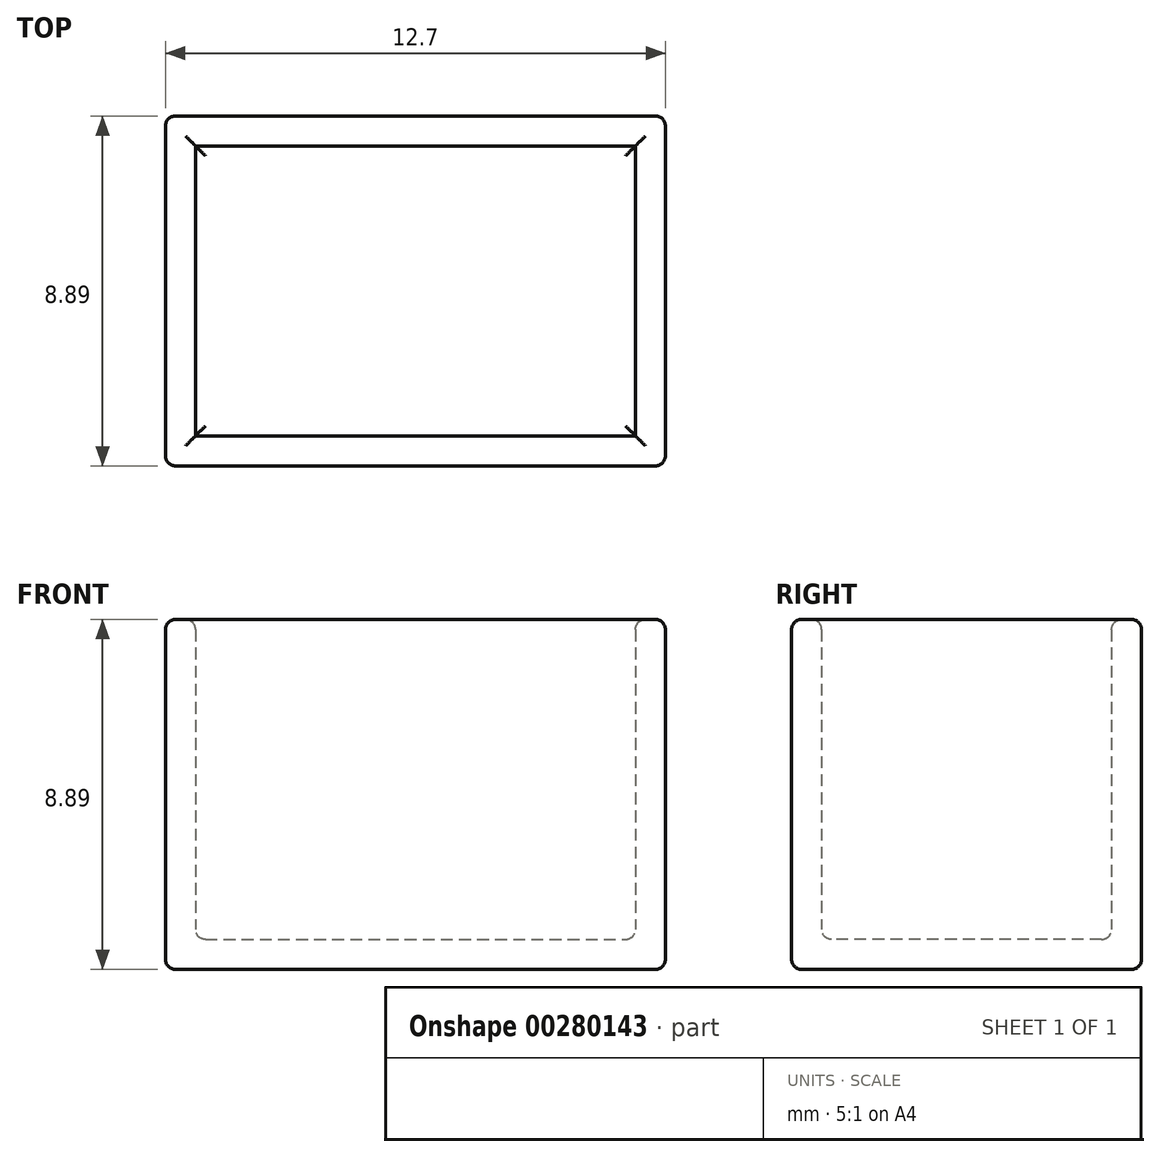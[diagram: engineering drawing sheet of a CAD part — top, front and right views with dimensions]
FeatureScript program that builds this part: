
annotation { "Feature Type Name" : "Feature", "Feature Type Description" : "" }
export const myFeature = defineFeature(function(context is Context, id is Id, definition is map)
    precondition{}
    {
        {
            var Q0;
            Q0=qCreatedBy(makeId("Top.planeOp"),FACE);
            var sketch = newSketch(context, id + "F0", { "sketchPlane" : qUnion([Q0])});
            skLineSegment(sketch, "E0.bottom", {"start": v(-47.71, 34.6) * mm, "end": v(-35.01, 34.6) * mm});
            skLineSegment(sketch, "E0.top", {"start": v(-47.71, 25.7) * mm, "end": v(-35.01, 25.7) * mm});
            skLineSegment(sketch, "E0.left", {"start": v(-47.71, 34.6) * mm, "end": v(-47.71, 25.7) * mm});
            skLineSegment(sketch, "E0.right", {"start": v(-35.01, 34.6) * mm, "end": v(-35.01, 25.7) * mm});
            skSolve(sketch);
        }
        {
            var Q0;
            Q0 = qSketchRegion(id + "F0", true);
            extrude(context, id + "F1", {"entities" : qUnion([Q0]), "depth" : 8.9 * mm});
        }
        {
            var Q0;
            Q0=makeQuery(id+"F1.opExtrude","CAP_FACE",FACE,{"disambiguationData":[OSD([sQuery(id+"F0.wireOp",EDGE,"E0.bottom"),sQuery(id+"F0.wireOp",EDGE,"E0.top"),sQuery(id+"F0.wireOp",EDGE,"E0.left"),sQuery(id+"F0.wireOp",EDGE,"E0.right")])],"isStart":false});
            shell(context, id + "F2", {"entities" : qUnion([Q0]), "thickness" : 0.76 * mm});
        }
        {
            var Q0;
            {var subQ0=sQuery(id+"F0.wireOp",EDGE,"E0.bottom");Q0=makeQuery(id+"F2.opShell","OFFSET_EDGE",EDGE,{"disambiguationData":[OSD([subQ0]),TDD([makeQuery(id+"F1.opExtrude","CAP_EDGE",EDGE,{"disambiguationData":[OSD([subQ0])],"isStart":false})])]});}
            var Q1;
            Q1=makeQuery(id+"F1.opExtrude","CAP_EDGE",EDGE,{"disambiguationData":[OSD([sQuery(id+"F0.wireOp",EDGE,"E0.top")])],"isStart":false});
            var Q2;
            {var subQ0=sQuery(id+"F0.wireOp",EDGE,"E0.top");Q2=makeQuery(id+"F2.opShell","OFFSET_EDGE",EDGE,{"disambiguationData":[OSD([subQ0]),TDD([makeQuery(id+"F1.opExtrude","CAP_EDGE",EDGE,{"disambiguationData":[OSD([subQ0])],"isStart":false})])]});}
            var Q3;
            Q3=makeQuery(id+"F1.opExtrude","CAP_EDGE",EDGE,{"disambiguationData":[OSD([sQuery(id+"F0.wireOp",EDGE,"E0.bottom")])],"isStart":false});
            var Q4;
            {var subQ0=sQuery(id+"F0.wireOp",EDGE,"E0.left");Q4=makeQuery(id+"F2.opShell","OFFSET_EDGE",EDGE,{"disambiguationData":[OSD([subQ0]),TDD([makeQuery(id+"F1.opExtrude","CAP_EDGE",EDGE,{"disambiguationData":[OSD([subQ0])],"isStart":false})])]});}
            var Q5;
            Q5=makeQuery(id+"F1.opExtrude","CAP_EDGE",EDGE,{"disambiguationData":[OSD([sQuery(id+"F0.wireOp",EDGE,"E0.left")])],"isStart":false});
            var Q6;
            {var subQ0=sQuery(id+"F0.wireOp",EDGE,"E0.right");Q6=makeQuery(id+"F2.opShell","OFFSET_EDGE",EDGE,{"disambiguationData":[OSD([subQ0]),TDD([makeQuery(id+"F1.opExtrude","CAP_EDGE",EDGE,{"disambiguationData":[OSD([subQ0])],"isStart":false})])]});}
            var Q7;
            Q7=makeQuery(id+"F1.opExtrude","CAP_EDGE",EDGE,{"disambiguationData":[OSD([sQuery(id+"F0.wireOp",EDGE,"E0.right")])],"isStart":false});
            var Q8;
            Q8=makeQuery(id+"F1.opExtrude","SWEPT_EDGE",EDGE,{"disambiguationData":[OSD([sQuery(id+"F0.wireOp",EDGE,"E0.top"),sQuery(id+"F0.wireOp",EDGE,"E0.right")])]});
            var Q9;
            Q9=makeQuery(id+"F1.opExtrude","SWEPT_EDGE",EDGE,{"disambiguationData":[OSD([sQuery(id+"F0.wireOp",EDGE,"E0.top"),sQuery(id+"F0.wireOp",EDGE,"E0.left")])]});
            var Q10;
            Q10=makeQuery(id+"F1.opExtrude","SWEPT_EDGE",EDGE,{"disambiguationData":[OSD([sQuery(id+"F0.wireOp",EDGE,"E0.bottom"),sQuery(id+"F0.wireOp",EDGE,"E0.left")])]});
            var Q11;
            Q11=makeQuery(id+"F1.opExtrude","SWEPT_EDGE",EDGE,{"disambiguationData":[OSD([sQuery(id+"F0.wireOp",EDGE,"E0.bottom"),sQuery(id+"F0.wireOp",EDGE,"E0.right")])]});
            var Q12;
            Q12=makeQuery(id+"F1.opExtrude","CAP_EDGE",EDGE,{"disambiguationData":[OSD([sQuery(id+"F0.wireOp",EDGE,"E0.right")])],"isStart":true});
            var Q13;
            Q13=makeQuery(id+"F1.opExtrude","CAP_EDGE",EDGE,{"disambiguationData":[OSD([sQuery(id+"F0.wireOp",EDGE,"E0.top")])],"isStart":true});
            var Q14;
            Q14=makeQuery(id+"F1.opExtrude","CAP_EDGE",EDGE,{"disambiguationData":[OSD([sQuery(id+"F0.wireOp",EDGE,"E0.left")])],"isStart":true});
            var Q15;
            Q15=makeQuery(id+"F1.opExtrude","CAP_EDGE",EDGE,{"disambiguationData":[OSD([sQuery(id+"F0.wireOp",EDGE,"E0.bottom")])],"isStart":true});
            fillet(context, id + "F3", {"entities" : qUnion([Q0, Q1, Q2, Q3, Q4, Q5, Q6, Q7, Q8, Q9, Q10, Q11, Q12, Q13, Q14, Q15]), "radius" : 0.25 * mm, "tangentPropagation" : true, "allowEdgeOverflow" : false});
        }
        {
            var Q0;
            {var subQ0=sQuery(id+"F0.wireOp",EDGE,"E0.bottom");Q0=makeQuery(id+"F2.opShell","OFFSET_EDGE",EDGE,{"disambiguationData":[OSD([subQ0]),TDD([makeQuery(id+"F1.opExtrude","CAP_EDGE",EDGE,{"disambiguationData":[OSD([subQ0])],"isStart":true})])]});}
            var Q1;
            {var subQ0=sQuery(id+"F0.wireOp",EDGE,"E0.right");Q1=makeQuery(id+"F2.opShell","OFFSET_EDGE",EDGE,{"disambiguationData":[OSD([subQ0]),TDD([makeQuery(id+"F1.opExtrude","CAP_EDGE",EDGE,{"disambiguationData":[OSD([subQ0])],"isStart":true})])]});}
            var Q2;
            {var subQ0=sQuery(id+"F0.wireOp",EDGE,"E0.top");Q2=makeQuery(id+"F2.opShell","OFFSET_EDGE",EDGE,{"disambiguationData":[OSD([subQ0]),TDD([makeQuery(id+"F1.opExtrude","CAP_EDGE",EDGE,{"disambiguationData":[OSD([subQ0])],"isStart":true})])]});}
            var Q3;
            {var subQ0=sQuery(id+"F0.wireOp",EDGE,"E0.left");Q3=makeQuery(id+"F2.opShell","OFFSET_EDGE",EDGE,{"disambiguationData":[OSD([subQ0]),TDD([makeQuery(id+"F1.opExtrude","CAP_EDGE",EDGE,{"disambiguationData":[OSD([subQ0])],"isStart":true})])]});}
            fillet(context, id + "F4", {"entities" : qUnion([Q0, Q1, Q2, Q3]), "radius" : 0.25 * mm, "tangentPropagation" : true, "allowEdgeOverflow" : false});
        }
    });
